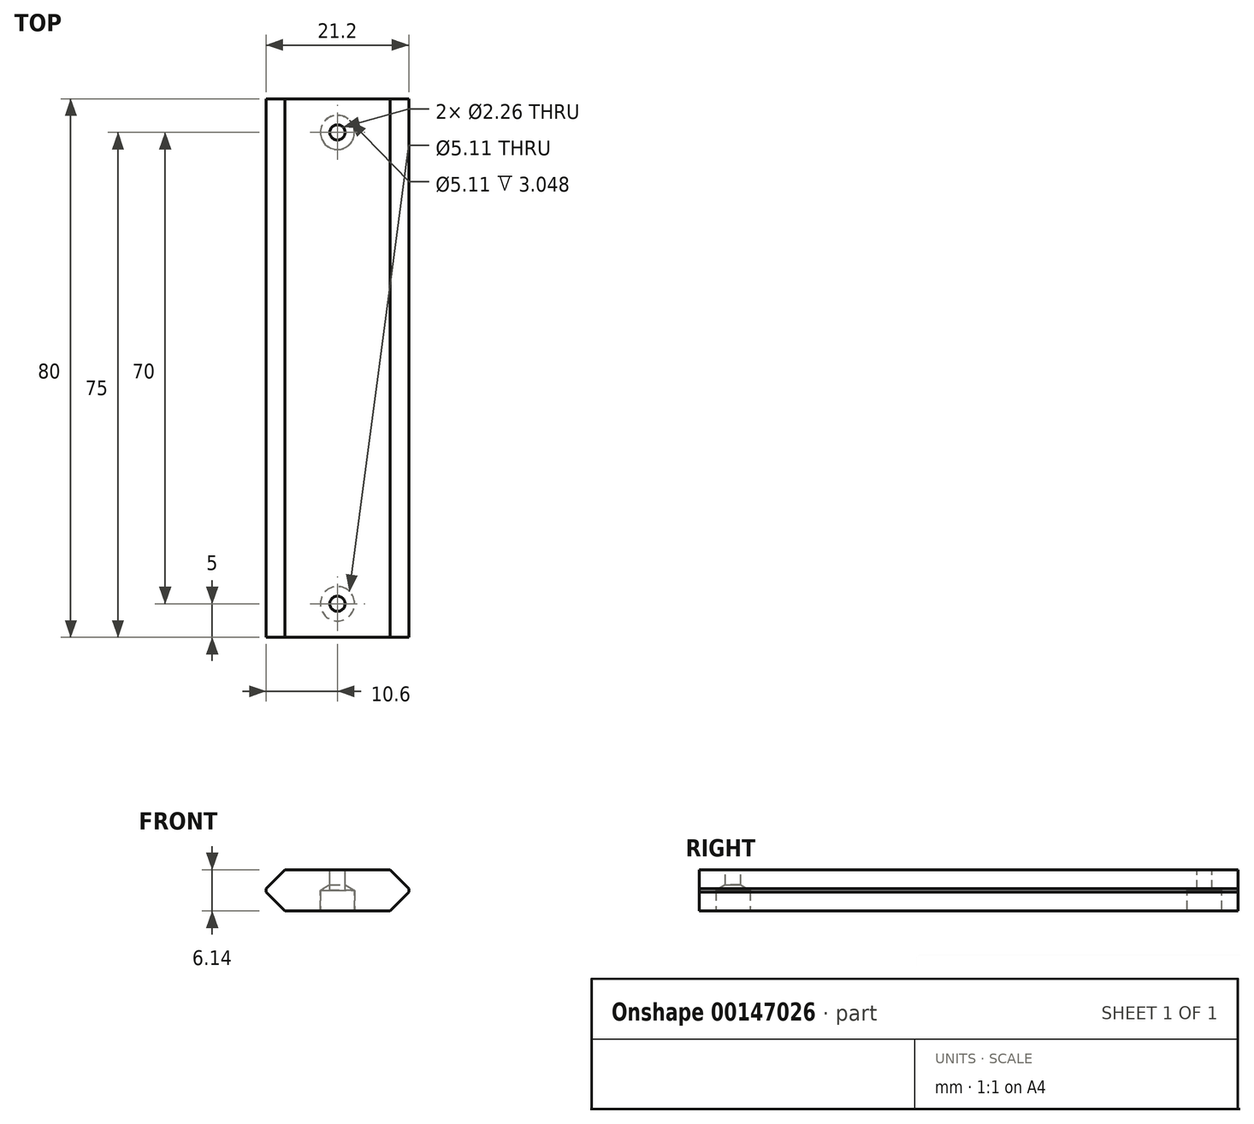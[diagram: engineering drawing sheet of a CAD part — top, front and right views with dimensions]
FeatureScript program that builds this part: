
annotation { "Feature Type Name" : "Feature", "Feature Type Description" : "" }
export const myFeature = defineFeature(function(context is Context, id is Id, definition is map)
    precondition{}
    {
        {
            var Q0;
            Q0=qCreatedBy(makeId("Front.planeOp"),FACE);
            var sketch = newSketch(context, id + "F0", { "sketchPlane" : qUnion([Q0])});
            skPoint(sketch, "E0.middle", {"position": v(0, 0) * mm});
            skLineSegment(sketch, "E1", {"start": v(-10.6, 0.27) * mm, "end": v(-7.8, 3.07) * mm});
            skLineSegment(sketch, "E2", {"start": v(-10.6, -0.27) * mm, "end": v(-7.8, -3.07) * mm});
            skLineSegment(sketch, "E3.0", {"start": v(0, -10.87) * mm, "end": v(0.03, -10.84) * mm});
            skLineSegment(sketch, "E4.0", {"start": v(0, 10.87) * mm, "end": v(0.03, 10.84) * mm});
            skLineSegment(sketch, "E5.bottom", {"start": v(0.03, 10.84) * mm, "end": v(-0.03, 10.84) * mm});
            skLineSegment(sketch, "E5.top", {"start": v(0.03, -10.84) * mm, "end": v(-0.03, -10.84) * mm});
            skLineSegment(sketch, "E5.left", {"start": v(10.6, 0.27) * mm, "end": v(10.6, -0.27) * mm});
            skLineSegment(sketch, "E5.right", {"start": v(-10.6, 0.27) * mm, "end": v(-10.6, -0.27) * mm});
            skLineSegment(sketch, "E6.bottom", {"start": v(7.8, 3.07) * mm, "end": v(-7.8, 3.07) * mm});
            skLineSegment(sketch, "E6.top", {"start": v(7.8, -3.07) * mm, "end": v(-7.8, -3.07) * mm});
            skLineSegment(sketch, "E7.trimOffspring", {"start": v(7.8, 3.07) * mm, "end": v(10.6, 0.27) * mm});
            skPoint(sketch, "E8.orphan", {"position": v(10.6, 10.84) * mm});
            skPoint(sketch, "E9.orphan", {"position": v(-10.6, 10.84) * mm});
            skPoint(sketch, "E10.orphan", {"position": v(-10.6, -10.84) * mm});
            skPoint(sketch, "E11.orphan", {"position": v(10.6, -10.84) * mm});
            skLineSegment(sketch, "E12", {"start": v(-0.03, 10.84) * mm, "end": v(0, 10.87) * mm});
            skLineSegment(sketch, "E13", {"start": v(-0.03, -10.84) * mm, "end": v(0, -10.87) * mm});
            skLineSegment(sketch, "E14", {"start": v(7.8, -3.07) * mm, "end": v(10.6, -0.27) * mm});
            skPoint(sketch, "E0.left.end.orphan", {"position": v(9.5, 1.37) * mm});
            skPoint(sketch, "E0.left.start.orphan", {"position": v(9.5, -1.37) * mm});
            skPoint(sketch, "E0.right.end.orphan", {"position": v(-9.5, 1.37) * mm});
            skPoint(sketch, "E0.bottom.end.orphan", {"position": v(-9.5, -1.37) * mm});
            skSolve(sketch);
        }
        {
            var Q0;
            Q0=makeQuery(id+"F0.imprint","IMPRINT",FACE,{"disambiguationData":[TD([[makeQuery(id+"F0.imprint","IMPRINT",EDGE,{"derivedFrom":sQuery(id+"F0.wireOp",EDGE,"E1")}),-1.0]])]});
            extrude(context, id + "F1", {"entities" : qUnion([Q0]), "endBound" : BoundingType.SYMMETRIC, "depth" : 80 * mm});
        }
        {
            var Q0;
            Q0=qCreatedBy(makeId("Front.planeOp"),FACE);
            cPlane(context, id + "F2", {"entities" : qUnion([Q0]), "cplaneType" : CPlaneType.OFFSET, "offset" : 35 * mm, "width" : 150 * mm, "height" : 150 * mm});
        }
        {
            var Q0;
            Q0=qCreatedBy(makeId("Front.planeOp"),FACE);
            cPlane(context, id + "F3", {"entities" : qUnion([Q0]), "cplaneType" : CPlaneType.OFFSET, "offset" : 35 * mm, "oppositeDirection" : true, "width" : 150 * mm, "height" : 150 * mm});
        }
        {
            var Q0;
            Q0=qCreatedBy(makeId("Top.planeOp"),FACE);
            var sketch = newSketch(context, id + "F4", { "sketchPlane" : qUnion([Q0])});
            skLineSegment(sketch, "E15", {"start": v(50.9, -35) * mm, "end": v(-52.64, -35) * mm});
            skLineSegment(sketch, "E16", {"start": v(0, 43.71) * mm, "end": v(0, -59.82) * mm});
            skLineSegment(sketch, "E17", {"start": v(103.85, 35) * mm, "end": v(-60.5, 35) * mm});
            skPoint(sketch, "E18", {"position": v(0, -35) * mm});
            skPoint(sketch, "E19", {"position": v(0, 35) * mm});
            skSolve(sketch);
        }
        {
            var Q0;
            Q0=sQuery(id+"F4.wireOp",VERTEX,"E18");
            var Q1;
            Q1=makeQuery(id+"F1.opExtrude","SWEPT_BODY",BODY,{"disambiguationData":[OSD([sQuery(id+"F0.wireOp",EDGE,"E1"),sQuery(id+"F0.wireOp",EDGE,"E2"),sQuery(id+"F0.wireOp",EDGE,"E5.left"),sQuery(id+"F0.wireOp",EDGE,"E5.right"),sQuery(id+"F0.wireOp",EDGE,"E6.bottom"),sQuery(id+"F0.wireOp",EDGE,"E6.top"),sQuery(id+"F0.wireOp",EDGE,"E7.trimOffspring"),sQuery(id+"F0.wireOp",EDGE,"E14")])]});
            hole(context, id + "F5", {"style" : HoleStyle.SIMPLE, "endStyle" : HoleEndStyle.THROUGH, "holeDiameter" : 2.26 * mm, "startFromSketch" : true, "locations" : qUnion([Q0]), "scope" : qUnion([Q1]), "isTappedThrough" : true});
        }
        {
            var Q0;
            Q0=sQuery(id+"F4.wireOp",VERTEX,"E18");
            var Q1;
            Q1=makeQuery(id+"F1.opExtrude","SWEPT_BODY",BODY,{"disambiguationData":[OSD([sQuery(id+"F0.wireOp",EDGE,"E1"),sQuery(id+"F0.wireOp",EDGE,"E2"),sQuery(id+"F0.wireOp",EDGE,"E5.left"),sQuery(id+"F0.wireOp",EDGE,"E5.right"),sQuery(id+"F0.wireOp",EDGE,"E6.bottom"),sQuery(id+"F0.wireOp",EDGE,"E6.top"),sQuery(id+"F0.wireOp",EDGE,"E7.trimOffspring"),sQuery(id+"F0.wireOp",EDGE,"E14")])]});
            hole(context, id + "F6", {"style" : HoleStyle.SIMPLE, "endStyle" : HoleEndStyle.THROUGH, "oppositeDirection" : true, "holeDiameter" : 2.26 * mm, "startFromSketch" : true, "locations" : qUnion([Q0]), "scope" : qUnion([Q1]), "isTappedThrough" : true});
        }
        {
            var Q0;
            Q0=sQuery(id+"F4.wireOp",VERTEX,"E19");
            var Q1;
            Q1=makeQuery(id+"F1.opExtrude","SWEPT_BODY",BODY,{"disambiguationData":[OSD([sQuery(id+"F0.wireOp",EDGE,"E1"),sQuery(id+"F0.wireOp",EDGE,"E2"),sQuery(id+"F0.wireOp",EDGE,"E5.left"),sQuery(id+"F0.wireOp",EDGE,"E5.right"),sQuery(id+"F0.wireOp",EDGE,"E6.bottom"),sQuery(id+"F0.wireOp",EDGE,"E6.top"),sQuery(id+"F0.wireOp",EDGE,"E7.trimOffspring"),sQuery(id+"F0.wireOp",EDGE,"E14")])]});
            hole(context, id + "F7", {"style" : HoleStyle.SIMPLE, "endStyle" : HoleEndStyle.THROUGH, "holeDiameter" : 2.26 * mm, "startFromSketch" : true, "locations" : qUnion([Q0]), "scope" : qUnion([Q1]), "isTappedThrough" : true});
        }
        {
            var Q0;
            Q0=sQuery(id+"F4.wireOp",VERTEX,"E19");
            var Q1;
            Q1=makeQuery(id+"F1.opExtrude","SWEPT_BODY",BODY,{"disambiguationData":[OSD([sQuery(id+"F0.wireOp",EDGE,"E1"),sQuery(id+"F0.wireOp",EDGE,"E2"),sQuery(id+"F0.wireOp",EDGE,"E5.left"),sQuery(id+"F0.wireOp",EDGE,"E5.right"),sQuery(id+"F0.wireOp",EDGE,"E6.bottom"),sQuery(id+"F0.wireOp",EDGE,"E6.top"),sQuery(id+"F0.wireOp",EDGE,"E7.trimOffspring"),sQuery(id+"F0.wireOp",EDGE,"E14")])]});
            hole(context, id + "F8", {"style" : HoleStyle.SIMPLE, "endStyle" : HoleEndStyle.THROUGH, "oppositeDirection" : true, "holeDiameter" : 2.26 * mm, "startFromSketch" : true, "locations" : qUnion([Q0]), "scope" : qUnion([Q1]), "isTappedThrough" : true});
        }
        {
            var Q0;
            Q0=qCreatedBy(makeId("Top.planeOp"),FACE);
            cPlane(context, id + "F9", {"entities" : qUnion([Q0]), "cplaneType" : CPlaneType.OFFSET, "offset" : (6.14 / 2) * mm, "oppositeDirection" : true, "width" : 150 * mm, "height" : 150 * mm});
        }
        {
            var Q0;
            Q0=qCreatedBy(id+"F9.planeOp",FACE);
            var sketch = newSketch(context, id + "F10", { "sketchPlane" : qUnion([Q0])});
            skCircle(sketch, "E20.0", {"center": v(0, -35) * mm, "radius": 1.13 * mm});
            skCircle(sketch, "E21.0", {"center": v(0, 35) * mm, "radius": 1.13 * mm});
            skSolve(sketch);
        }
        {
            var Q0;
            Q0=sQuery(id+"F10.wireOp",VERTEX,"E20.0.center");
            var Q1;
            Q1=makeQuery(id+"F1.opExtrude","SWEPT_BODY",BODY,{"disambiguationData":[OSD([sQuery(id+"F0.wireOp",EDGE,"E1"),sQuery(id+"F0.wireOp",EDGE,"E2"),sQuery(id+"F0.wireOp",EDGE,"E5.left"),sQuery(id+"F0.wireOp",EDGE,"E5.right"),sQuery(id+"F0.wireOp",EDGE,"E6.bottom"),sQuery(id+"F0.wireOp",EDGE,"E6.top"),sQuery(id+"F0.wireOp",EDGE,"E7.trimOffspring"),sQuery(id+"F0.wireOp",EDGE,"E14")])]});
            hole(context, id + "F11", {"style" : HoleStyle.SIMPLE, "endStyle" : HoleEndStyle.BLIND, "oppositeDirection" : true, "holeDiameter" : 5.1 * mm, "holeDepth" : 3.05 * mm, "startFromSketch" : true, "locations" : qUnion([Q0]), "scope" : qUnion([Q1])});
        }
        {
            var Q0;
            Q0=sQuery(id+"F4.wireOp",VERTEX,"E19");
            var Q1;
            Q1=makeQuery(id+"F1.opExtrude","SWEPT_BODY",BODY,{"disambiguationData":[OSD([sQuery(id+"F0.wireOp",EDGE,"E1"),sQuery(id+"F0.wireOp",EDGE,"E2"),sQuery(id+"F0.wireOp",EDGE,"E5.left"),sQuery(id+"F0.wireOp",EDGE,"E5.right"),sQuery(id+"F0.wireOp",EDGE,"E6.bottom"),sQuery(id+"F0.wireOp",EDGE,"E6.top"),sQuery(id+"F0.wireOp",EDGE,"E7.trimOffspring"),sQuery(id+"F0.wireOp",EDGE,"E14")])]});
            hole(context, id + "F12", {"style" : HoleStyle.SIMPLE, "endStyle" : HoleEndStyle.BLIND, "holeDiameter" : 5.1 * mm, "holeDepth" : 3.05 * mm, "startFromSketch" : true, "locations" : qUnion([Q0]), "scope" : qUnion([Q1])});
        }
    });
